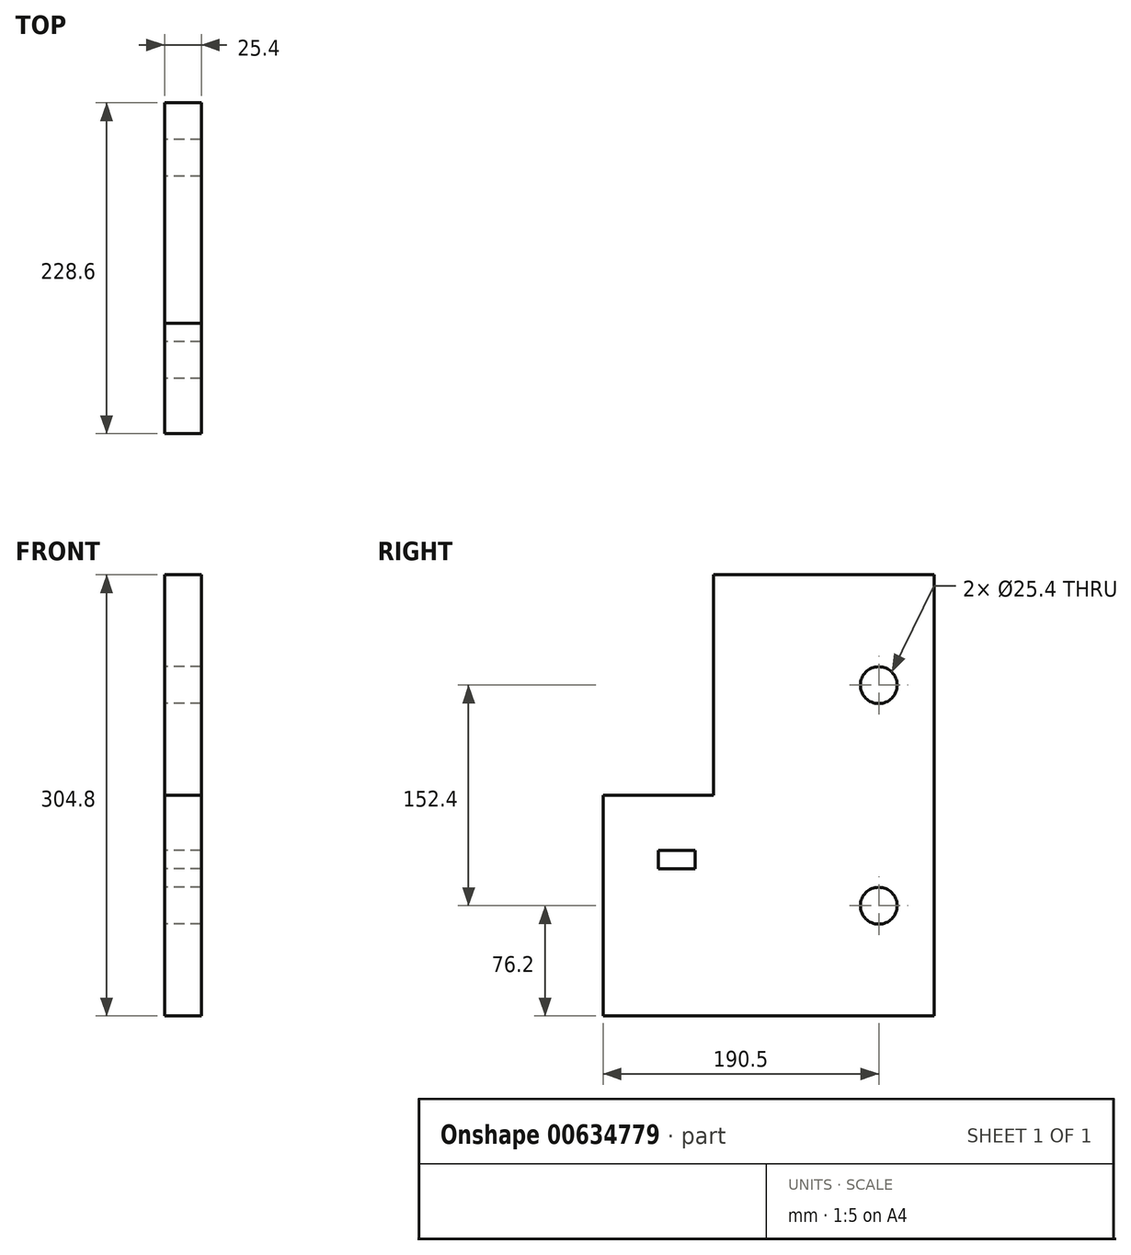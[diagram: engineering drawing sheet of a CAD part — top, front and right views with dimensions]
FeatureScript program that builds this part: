
annotation { "Feature Type Name" : "Feature", "Feature Type Description" : "" }
export const myFeature = defineFeature(function(context is Context, id is Id, definition is map)
    precondition{}
    {
        {
            var Q0;
            Q0=qCreatedBy(makeId("Right.planeOp"),FACE);
            var sketch = newSketch(context, id + "F0", { "sketchPlane" : qUnion([Q0])});
            skLineSegment(sketch, "E0.bottom", {"start": v(114.3, 152.4) * mm, "end": v(-38.1, 152.4) * mm});
            skLineSegment(sketch, "E0.top", {"start": v(114.3, -152.4) * mm, "end": v(-114.3, -152.4) * mm});
            skLineSegment(sketch, "E0.left", {"start": v(114.3, 152.4) * mm, "end": v(114.3, -152.4) * mm});
            skLineSegment(sketch, "E0.right", {"start": v(-114.3, 0) * mm, "end": v(-114.3, -152.4) * mm});
            skPoint(sketch, "E0.middle", {"position": v(0, 0) * mm});
            skLineSegment(sketch, "E1.top", {"start": v(-114.3, 0) * mm, "end": v(-38.1, 0) * mm});
            skLineSegment(sketch, "E1.right", {"start": v(-38.1, 152.4) * mm, "end": v(-38.1, 0) * mm});
            skPoint(sketch, "E2.orphan", {"position": v(-114.3, 152.4) * mm});
            skCircle(sketch, "E3", {"center": v(76.2, 76.2) * mm, "radius": 12.7 * mm});
            skCircle(sketch, "E4", {"center": v(76.2, -76.2) * mm, "radius": 12.7 * mm});
            skSolve(sketch);
        }
        {
            var Q0;
            Q0 = qSketchRegion(id + "F0", true);
            extrude(context, id + "F1", {"entities" : qUnion([Q0]), "depth" : 25.4 * mm, "offsetDistance" : 25.4 * mm});
        }
        {
            var Q0;
            Q0=makeQuery(id+"F1.opExtrude","CAP_FACE",FACE,{"disambiguationData":[OSD([sQuery(id+"F0.wireOp",EDGE,"E0.bottom"),sQuery(id+"F0.wireOp",EDGE,"E0.top"),sQuery(id+"F0.wireOp",EDGE,"E0.left"),sQuery(id+"F0.wireOp",EDGE,"E0.right"),sQuery(id+"F0.wireOp",EDGE,"E1.top"),sQuery(id+"F0.wireOp",EDGE,"E1.right"),sQuery(id+"F0.wireOp",EDGE,"E3"),sQuery(id+"F0.wireOp",EDGE,"E4")])],"isStart":true});
            var sketch = newSketch(context, id + "F2", { "sketchPlane" : qUnion([Q0])});
            skLineSegment(sketch, "E5.bottom", {"start": v(50.8, -38.1) * mm, "end": v(76.2, -38.1) * mm});
            skLineSegment(sketch, "E5.top", {"start": v(50.8, -50.8) * mm, "end": v(76.2, -50.8) * mm});
            skLineSegment(sketch, "E5.left", {"start": v(50.8, -38.1) * mm, "end": v(50.8, -50.8) * mm});
            skLineSegment(sketch, "E5.right", {"start": v(76.2, -38.1) * mm, "end": v(76.2, -50.8) * mm});
            skSolve(sketch);
        }
        {
            var Q0;
            Q0 = qSketchRegion(id + "F2", true);
            extrude(context, id + "F3", {"entities" : qUnion([Q0]), "operationType" : NewBodyOperationType.REMOVE, "oppositeDirection" : true, "depth" : 25.4 * mm, "offsetDistance" : 25.4 * mm});
        }
    });
